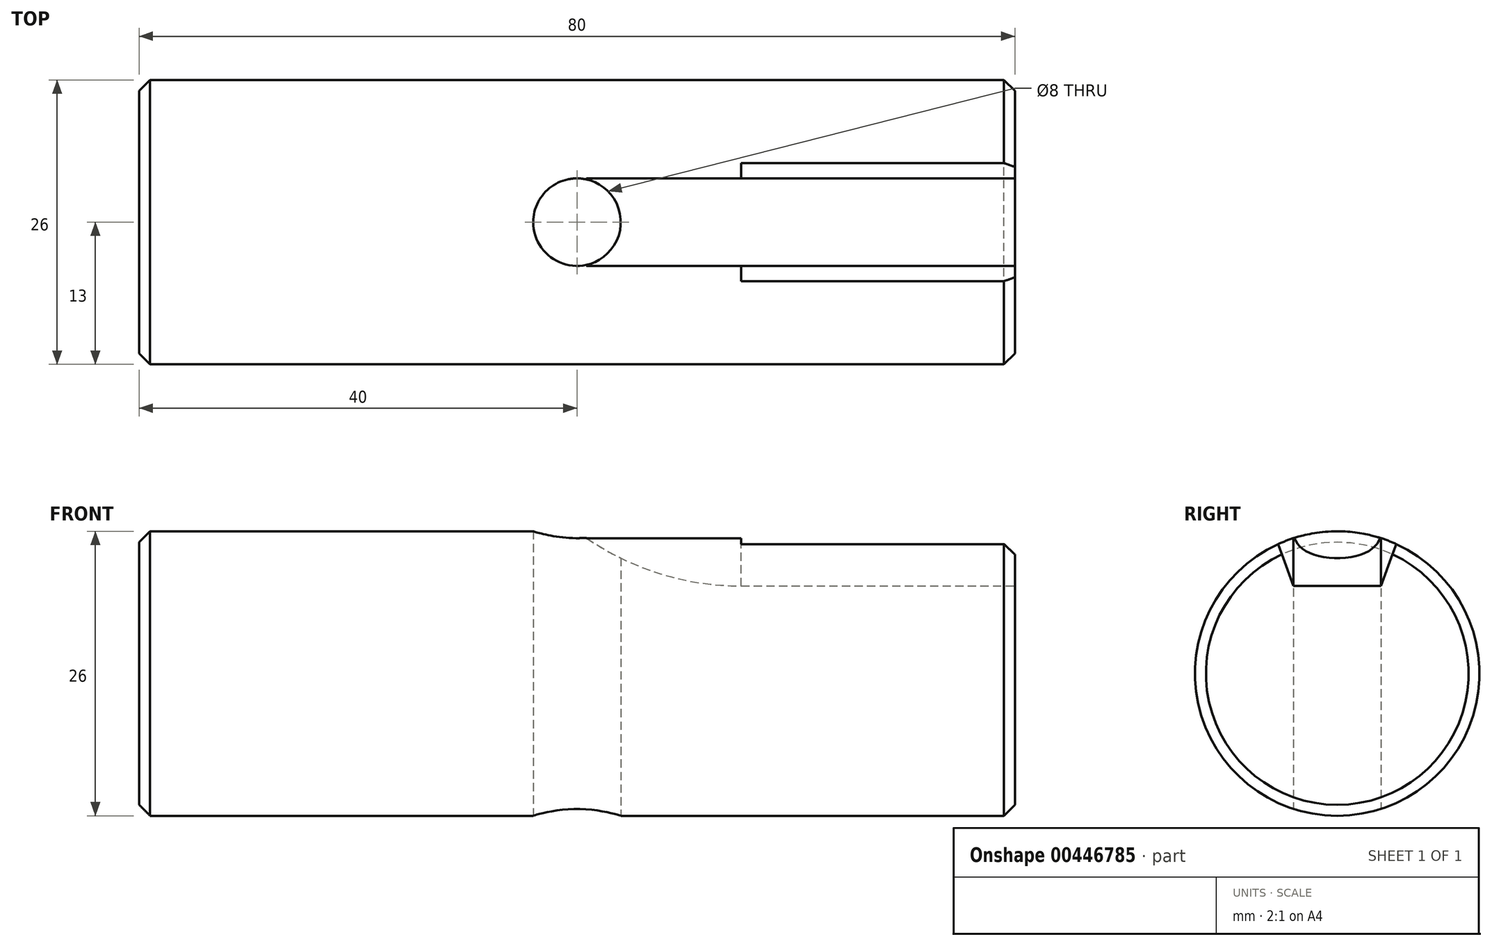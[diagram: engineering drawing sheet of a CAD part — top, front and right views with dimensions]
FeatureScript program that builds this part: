
annotation { "Feature Type Name" : "Feature", "Feature Type Description" : "" }
export const myFeature = defineFeature(function(context is Context, id is Id, definition is map)
    precondition{}
    {
        {
            var Q0;
            Q0=qCreatedBy(makeId("Right.planeOp"),FACE);
            var sketch = newSketch(context, id + "F0", { "sketchPlane" : qUnion([Q0])});
            skCircle(sketch, "E0", {"center": v(0, 0) * mm, "radius": 13 * mm});
            skSolve(sketch);
        }
        {
            var Q0;
            Q0 = qSketchRegion(id + "F0", true);
            extrude(context, id + "F1", {"entities" : qUnion([Q0]), "depth" : 80 * mm, "symmetric" : true});
        }
        {
            var Q0;
            Q0=qCreatedBy(makeId("Top.planeOp"),FACE);
            var sketch = newSketch(context, id + "F2", { "sketchPlane" : qUnion([Q0])});
            skCircle(sketch, "E1", {"center": v(0, 0) * mm, "radius": 4 * mm});
            skSolve(sketch);
        }
        {
            var Q0;
            Q0 = qSketchRegion(id + "F2", true);
            extrude(context, id + "F3", {"entities" : qUnion([Q0]), "operationType" : NewBodyOperationType.REMOVE, "depth" : 26 * mm, "symmetric" : true});
        }
        {
            var Q0;
            Q0=makeQuery(id+"F1.opExtrude","CAP_EDGE",EDGE,{"disambiguationData":[OSD([sQuery(id+"F0.wireOp",EDGE,"E0")])],"isStart":true});
            var Q1;
            Q1=makeQuery(id+"F1.opExtrude","CAP_EDGE",EDGE,{"disambiguationData":[OSD([sQuery(id+"F0.wireOp",EDGE,"E0")])],"isStart":false});
            chamfer(context, id + "F4", {"entities" : qUnion([Q0, Q1]), "width" : 1 * mm, "tangentPropagation" : true});
        }
        {
            var Q0;
            Q0=qCreatedBy(makeId("Front.planeOp"),FACE);
            var sketch = newSketch(context, id + "F5", { "sketchPlane" : qUnion([Q0])});
            skArc(sketch, "E2", {"start": v(0, 13) * mm, "mid": v(7.1, 9.28) * mm, "end": v(15, 8) * mm});
            skLineSegment(sketch, "E3", {"start": v(15, 8) * mm, "end": v(40, 8) * mm});
            skLineSegment(sketch, "E4.0", {"start": v(40, 12) * mm, "end": v(40, 8) * mm});
            skLineSegment(sketch, "E5", {"start": v(39, 13) * mm, "end": v(40, 12) * mm});
            skLineSegment(sketch, "E6", {"start": v(0, 13) * mm, "end": v(39, 13) * mm});
            skLineSegment(sketch, "E7", {"start": v(39, -13) * mm, "end": v(-39, -13) * mm});
            skPoint(sketch, "E8.orphan", {"position": v(40, -12) * mm});
            skSolve(sketch);
        }
        {
            var Q0;
            Q0 = qSketchRegion(id + "F5", true);
            extrude(context, id + "F6", {"entities" : qUnion([Q0]), "operationType" : NewBodyOperationType.REMOVE, "oppositeDirection" : true, "depth" : 8 * mm, "symmetric" : true});
        }
        {
            var Q0;
            Q0=makeQuery(id+"F1.opExtrude","CAP_FACE",FACE,{"disambiguationData":[OSD([sQuery(id+"F0.wireOp",EDGE,"E0")])],"isStart":false});
            var sketch = newSketch(context, id + "F7", { "sketchPlane" : qUnion([Q0])});
            skArc(sketch, "E9.0", {"start": v(4, 12.37) * mm, "mid": v(4.7, 12.12) * mm, "end": v(5.4, 11.83) * mm});
            skLineSegment(sketch, "E10", {"start": v(4, 8) * mm, "end": v(5.4, 11.83) * mm});
            skLineSegment(sketch, "E11", {"start": v(0, 0) * mm, "end": v(0, 5.1) * mm, "construction": true});
            skLineSegment(sketch, "E12.MirrorCS", {"start": v(-4, 8) * mm, "end": v(-5.4, 11.83) * mm});
            skArc(sketch, "E13.trimOffspring", {"start": v(-5.4, 11.83) * mm, "mid": v(-4.7, 12.12) * mm, "end": v(-4, 12.37) * mm});
            skLineSegment(sketch, "E14", {"start": v(4, 8) * mm, "end": v(4, 12.37) * mm});
            skLineSegment(sketch, "E15", {"start": v(-4, 8) * mm, "end": v(-4, 12.37) * mm});
            skPoint(sketch, "E16.0.end.orphan", {"position": v(3.91, 12.4) * mm});
            skPoint(sketch, "E16.0.start.orphan", {"position": v(-3.91, 12.4) * mm});
            skSolve(sketch);
        }
        {
            var Q0;
            Q0 = qSketchRegion(id + "F7", true);
            extrude(context, id + "F8", {"entities" : qUnion([Q0]), "operationType" : NewBodyOperationType.REMOVE, "oppositeDirection" : true, "depth" : 25 * mm});
        }
    });
